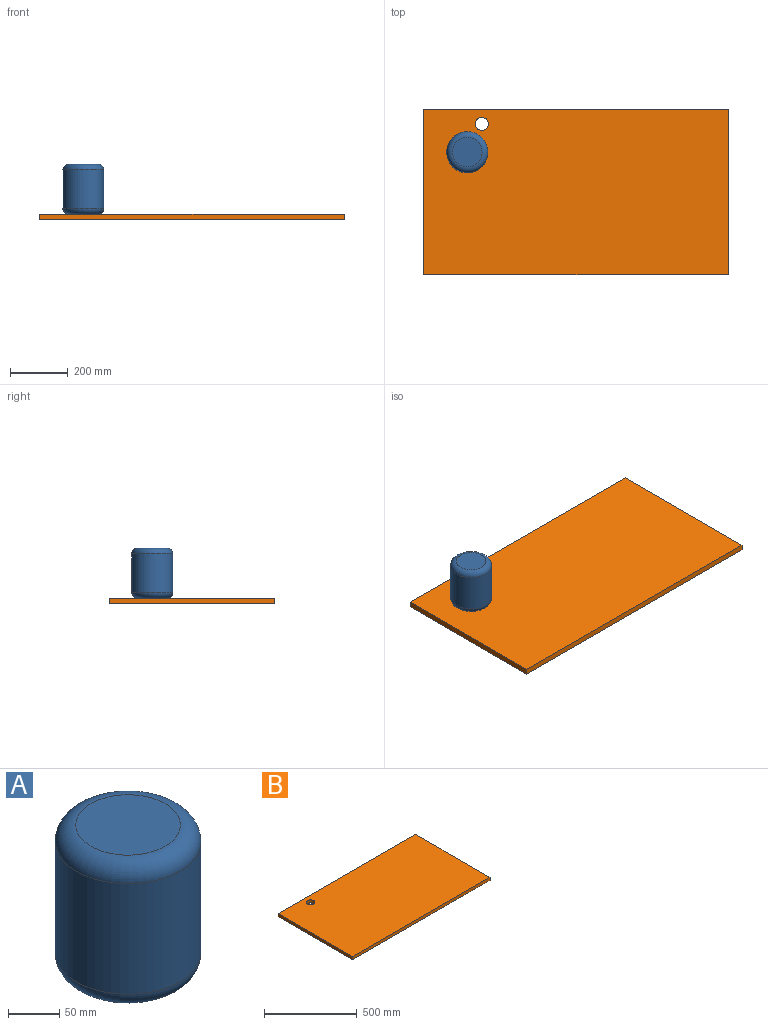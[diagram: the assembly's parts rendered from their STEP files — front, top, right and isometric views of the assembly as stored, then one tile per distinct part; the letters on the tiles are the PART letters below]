
ASSEMBLY  parts=2 mates=1
PART A: 5 faces, bbox 153.7x153.7x172 mm
  f0: cylinder r=71mm len=142mm, axis (0,0,-1), area 58886mm2, adj f3,f4
  f1: plane 102x102mm, normal (0,0,1), area 8171.3mm2, adj f4
  f2: plane 102x102mm, normal (0,0,-1), area 8171.3mm2, adj f3
  f3: torus R=51mm, axis (0,0,1), area 12580.3mm2, adj f0,f2
  f4: torus R=51mm, axis (0,0,1), area 12580.3mm2, adj f0,f1
PART B: 7 faces, bbox 1050x570x20 mm
  f0: plane 1050x20mm, normal (0,1,0), area 21000mm2, adj f1,f3,f4,f5
  f1: plane 570x20mm, normal (-1,0,0), area 11400mm2, adj f0,f2,f4,f5
  f2: plane 1050x20mm, normal (0,-1,0), area 21000mm2, adj f1,f3,f4,f5
  f3: plane 570x20mm, normal (1,0,0), area 11400mm2, adj f0,f2,f4,f5
  f4: plane 1050x570mm, normal (0,0,1), area 596909.6mm2, adj f0,f1,f2,f3,f6
  f5: plane 1050x570mm, normal (0,0,-1), area 596909.6mm2, adj f0,f1,f2,f3,f6
  f6: cylinder r=22.5mm len=45mm, axis (0,0,1), area 2827.4mm2, adj f4,f5
PLACE A t=(-157,127.59,-119.8)mm
PLACE B t=(-306.77,275.59,-139.8)mm fixed
MATE planar A.f0 <-> B.f4  axis (0,0,-1) through (-157,127.59,-119.8)mm
